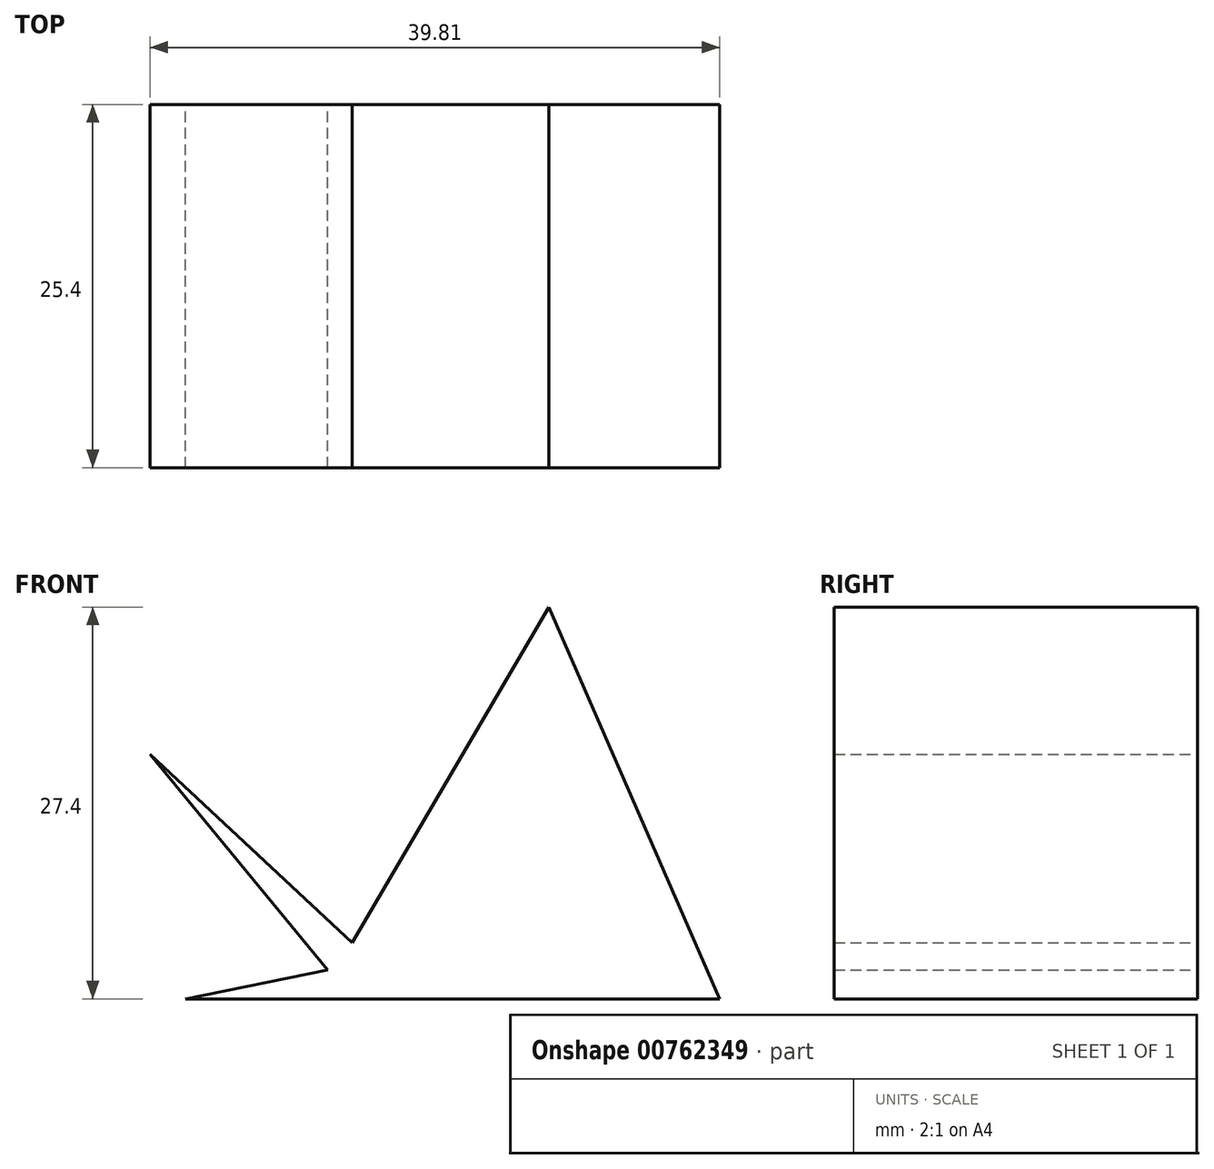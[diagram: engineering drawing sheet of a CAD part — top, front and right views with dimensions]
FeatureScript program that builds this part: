
annotation { "Feature Type Name" : "Feature", "Feature Type Description" : "" }
export const myFeature = defineFeature(function(context is Context, id is Id, definition is map)
    precondition{}
    {
        {
            var Q0;
            Q0=qCreatedBy(makeId("Front.planeOp"),FACE);
            var sketch = newSketch(context, id + "F0", { "sketchPlane" : qUnion([Q0])});
            skLineSegment(sketch, "E0", {"start": v(-37.33, 0) * mm, "end": v(0, 0) * mm});
            skLineSegment(sketch, "E1", {"start": v(0, 0) * mm, "end": v(-11.93, 27.4) * mm});
            skLineSegment(sketch, "E2", {"start": v(-11.93, 27.4) * mm, "end": v(-25.68, 3.91) * mm});
            skLineSegment(sketch, "E3", {"start": v(-25.68, 3.91) * mm, "end": v(-39.81, 17.1) * mm});
            skLineSegment(sketch, "E4", {"start": v(-39.81, 17.1) * mm, "end": v(-27.4, 2) * mm});
            skLineSegment(sketch, "E5", {"start": v(-27.4, 2) * mm, "end": v(-37.33, 0) * mm});
            skSolve(sketch);
        }
        {
            var Q0;
            Q0=makeQuery(id+"F0.imprint","IMPRINT",FACE,{"disambiguationData":[TD([[makeQuery(id+"F0.imprint","IMPRINT",EDGE,{"derivedFrom":sQuery(id+"F0.wireOp",EDGE,"E0")}),1.0]])]});
            extrude(context, id + "F1", {"entities" : qUnion([Q0]), "depth" : 25.4 * mm, "offsetDistance" : 25.4 * mm});
        }
    });
